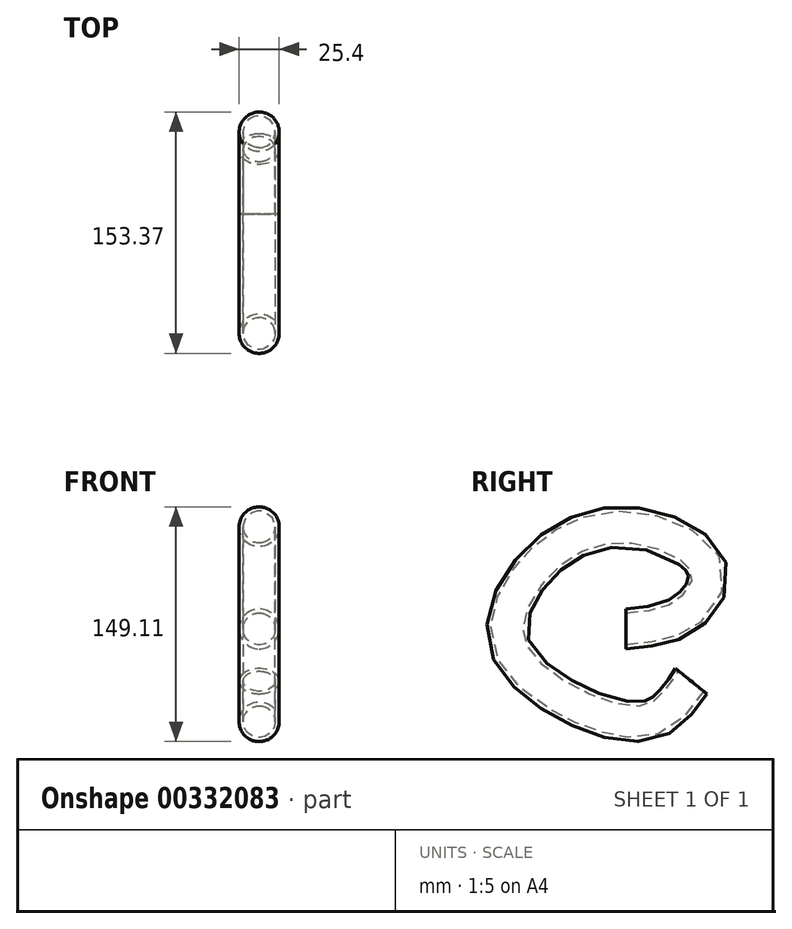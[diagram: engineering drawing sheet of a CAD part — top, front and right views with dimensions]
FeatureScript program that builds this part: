
annotation { "Feature Type Name" : "Feature", "Feature Type Description" : "" }
export const myFeature = defineFeature(function(context is Context, id is Id, definition is map)
    precondition{}
    {
        {
            var Q0;
            Q0=qCreatedBy(makeId("Front.planeOp"),FACE);
            var sketch = newSketch(context, id + "F0", { "sketchPlane" : qUnion([Q0])});
            skCircle(sketch, "E0", {"center": v(0, 0) * mm, "radius": 12.7 * mm});
            skSolve(sketch);
        }
        {
            var Q0;
            Q0=qCreatedBy(makeId("Right.planeOp"),FACE);
            var sketch = newSketch(context, id + "F1", { "sketchPlane" : qUnion([Q0])});
            skFitSpline(sketch, "E1", {"points": [v(0, 0) * mm, v(37.89, 9.88) * mm, v(51.54, 38.36) * mm, v(6.59, 64.24) * mm, v(-49.18, 47.3) * mm, v(-75.54, -3.77) * mm, v(-39.77, -44.24) * mm, v(15.77, -57.65) * mm, v(41.42, -33.18) * mm], "startDerivative": vector(359.68, 32.4) * mm, "endDerivative": vector(195.78, 292.72) * mm});
            skSolve(sketch);
        }
        {
            var Q0;
            Q0=makeQuery(id+"F0.imprint","IMPRINT",FACE,{"disambiguationData":[TD([[makeQuery(id+"F0.imprint","IMPRINT",EDGE,{"derivedFrom":sQuery(id+"F0.wireOp",EDGE,"E0")}),1.0]])]});
            var Q1;
            Q1=sQuery(id+"F1.wireOp",EDGE,"E1");
            sweep(context, id + "F2", {"profiles" : qUnion([Q0]), "path" : qUnion([Q1])});
        }
        {
            var Q0;
            Q0=makeQuery(id+"F2.opSweep","CAP_FACE",FACE,{"disambiguationData":[OSD([sQuery(id+"F0.wireOp",EDGE,"E0"),sQuery(id+"F1.wireOp",VERTEX,"E1.end")])],"isStart":false});
            var Q1;
            Q1=makeQuery(id+"F2.opSweep","CAP_FACE",FACE,{"disambiguationData":[OSD([sQuery(id+"F0.wireOp",EDGE,"E0"),sQuery(id+"F1.wireOp",VERTEX,"E1.start")])],"isStart":true});
            shell(context, id + "F3", {"entities" : qUnion([Q0, Q1]), "thickness" : 2.54 * mm});
        }
    });
